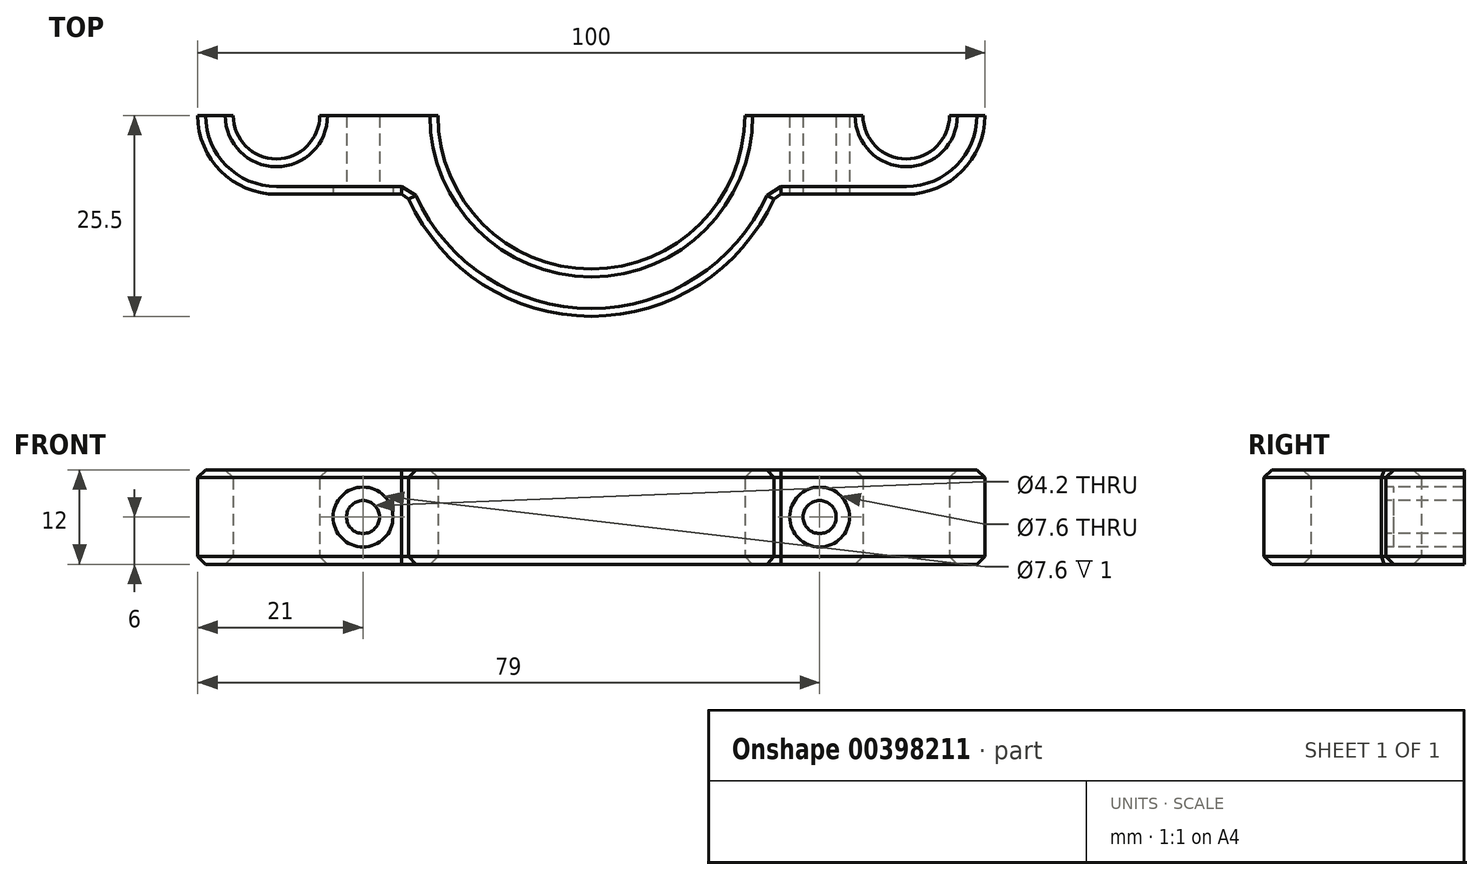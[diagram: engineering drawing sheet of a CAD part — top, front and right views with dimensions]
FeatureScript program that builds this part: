
annotation { "Feature Type Name" : "Feature", "Feature Type Description" : "" }
export const myFeature = defineFeature(function(context is Context, id is Id, definition is map)
    precondition{}
    {
        {
            var Q0;
            Q0=qCreatedBy(makeId("Top.planeOp"),FACE);
            var sketch = newSketch(context, id + "F0", { "sketchPlane" : qUnion([Q0])});
            skArc(sketch, "E0", {"start": v(-19.5, 0) * mm, "mid": v(0, -19.5) * mm, "end": v(19.5, 0) * mm});
            skArc(sketch, "E1", {"start": v(-50, 0) * mm, "mid": v(-47.07, -7.07) * mm, "end": v(-40, -10) * mm});
            skArc(sketch, "E2", {"start": v(-45.5, 0) * mm, "mid": v(-40, -5.5) * mm, "end": v(-34.5, 0) * mm});
            skArc(sketch, "E3.MirrorC", {"start": v(50, 0) * mm, "mid": v(47.07, -7.07) * mm, "end": v(40, -10) * mm});
            skArc(sketch, "E4.MirrorC", {"start": v(45.5, 0) * mm, "mid": v(40, -5.5) * mm, "end": v(34.5, 0) * mm});
            skArc(sketch, "E5", {"start": v(-23.46, -10) * mm, "mid": v(0, -25.5) * mm, "end": v(23.46, -10) * mm});
            skLineSegment(sketch, "E6", {"start": v(-40, -10) * mm, "end": v(-23.46, -10) * mm});
            skLineSegment(sketch, "E7", {"start": v(0, 0) * mm, "end": v(0, 37.42) * mm, "construction": true});
            skLineSegment(sketch, "E8.MirrorCS", {"start": v(40, -10) * mm, "end": v(23.46, -10) * mm});
            skLineSegment(sketch, "E9", {"start": v(-50, 0) * mm, "end": v(-45.5, 0) * mm});
            skLineSegment(sketch, "E10", {"start": v(-34.5, 0) * mm, "end": v(-19.5, 0) * mm});
            skLineSegment(sketch, "E11", {"start": v(19.5, 0) * mm, "end": v(34.5, 0) * mm});
            skLineSegment(sketch, "E12", {"start": v(45.5, 0) * mm, "end": v(50, 0) * mm});
            skSolve(sketch);
        }
        {
            var Q0;
            Q0=makeQuery(id+"F0.imprint","IMPRINT",FACE,{"disambiguationData":[TD([[makeQuery(id+"F0.imprint","IMPRINT",EDGE,{"derivedFrom":sQuery(id+"F0.wireOp",EDGE,"E0")}),-1.0]])]});
            var Q1;
            {var subQ0=sQuery(id+"F0.wireOp",EDGE,"9bc22d5b-6fa5-4b97-bc0c-ba3c2ce5b15b0.MirrorCS");var subQ1=sQuery(id+"F0.wireOp",EDGE,"E3.MirrorC");var subQ2=makeQuery(id+"F0.imprint","INTERSECT",VERTEX,{"derivedFrom":[subQ1,subQ0]});Q1=makeQuery(id+"F0.imprint","IMPRINT",FACE,{"disambiguationData":[TD([[makeQuery(id+"F0.imprint","IMPRINT",EDGE,{"disambiguationData":[TD([[subQ2,1.0]])],"derivedFrom":subQ1}),1.0]])]});}
            var Q2;
            {var subQ14=sQuery(id+"F0.wireOp",EDGE,"E3.MirrorC");var subQ15=makeQuery(id+"F0.imprint","INTERSECT",VERTEX,{"derivedFrom":[subQ14,sQuery(id+"F0.wireOp",EDGE,"9bc22d5b-6fa5-4b97-bc0c-ba3c2ce5b15b0.MirrorCS")]});Q2=makeQuery(id+"F0.imprint","IMPRINT",FACE,{"disambiguationData":[TD([[makeQuery(id+"F0.imprint","IMPRINT",EDGE,{"disambiguationData":[TD([[subQ15,-1.0]])],"derivedFrom":subQ14}),-1.0]])]});}
            var Q3;
            {var subQ0=sQuery(id+"F0.wireOp",EDGE,"c5e9826a-44c9-41ee-b3f6-7a52f2a30a6d0.MirrorCS");var subQ1=sQuery(id+"F0.wireOp",EDGE,"70cdf20a-ec98-4725-8234-b4e8db4446470.MirrorC");var subQ2=makeQuery(id+"F0.imprint","INTERSECT",VERTEX,{"disambiguationData":[OD(1.0)],"derivedFrom":[subQ1,subQ0]});Q3=makeQuery(id+"F0.imprint","IMPRINT",FACE,{"disambiguationData":[TD([[makeQuery(id+"F0.imprint","IMPRINT",EDGE,{"disambiguationData":[TD([[subQ2,-1.0]])],"derivedFrom":subQ1}),1.0]])]});}
            var Q4;
            {var subQ0=sQuery(id+"F0.wireOp",EDGE,"293a57c4-25d2-4a23-87fe-edfcddb039070.MirrorCS");var subQ1=sQuery(id+"F0.wireOp",EDGE,"70cdf20a-ec98-4725-8234-b4e8db4446470.MirrorC");var subQ2=makeQuery(id+"F0.imprint","INTERSECT",VERTEX,{"disambiguationData":[OD(1.0)],"derivedFrom":[subQ1,subQ0]});Q4=makeQuery(id+"F0.imprint","IMPRINT",FACE,{"disambiguationData":[TD([[makeQuery(id+"F0.imprint","IMPRINT",EDGE,{"disambiguationData":[TD([[subQ2,-1.0]])],"derivedFrom":subQ1}),1.0]])]});}
            var Q5;
            {var subQ0=sQuery(id+"F0.wireOp",EDGE,"8d17e300-eea9-4d37-96eb-c0b79c24fea70.MirrorCS");var subQ1=sQuery(id+"F0.wireOp",EDGE,"70cdf20a-ec98-4725-8234-b4e8db4446470.MirrorC");var subQ2=makeQuery(id+"F0.imprint","INTERSECT",VERTEX,{"disambiguationData":[OD(0.0)],"derivedFrom":[subQ1,subQ0]});Q5=makeQuery(id+"F0.imprint","IMPRINT",FACE,{"disambiguationData":[TD([[makeQuery(id+"F0.imprint","IMPRINT",EDGE,{"disambiguationData":[TD([[subQ2,1.0]])],"derivedFrom":subQ1}),1.0]])]});}
            var Q6;
            {var subQ0=sQuery(id+"F0.wireOp",EDGE,"8d17e300-eea9-4d37-96eb-c0b79c24fea70.MirrorCS");var subQ1=sQuery(id+"F0.wireOp",EDGE,"70cdf20a-ec98-4725-8234-b4e8db4446470.MirrorC");var subQ2=makeQuery(id+"F0.imprint","INTERSECT",VERTEX,{"disambiguationData":[OD(1.0)],"derivedFrom":[subQ1,subQ0]});Q6=makeQuery(id+"F0.imprint","IMPRINT",FACE,{"disambiguationData":[TD([[makeQuery(id+"F0.imprint","IMPRINT",EDGE,{"disambiguationData":[TD([[subQ2,-1.0]])],"derivedFrom":subQ1}),1.0]])]});}
            var Q7;
            {var subQ0=sQuery(id+"F0.wireOp",EDGE,"SkgDyUrd-1QQ2-iocv-R5lc-BY230uEkNkBm");var subQ1=sQuery(id+"F0.wireOp",EDGE,"E1");var subQ2=makeQuery(id+"F0.imprint","INTERSECT",VERTEX,{"derivedFrom":[subQ1,subQ0]});Q7=makeQuery(id+"F0.imprint","IMPRINT",FACE,{"disambiguationData":[TD([[makeQuery(id+"F0.imprint","IMPRINT",EDGE,{"disambiguationData":[TD([[subQ2,1.0]])],"derivedFrom":subQ1}),-1.0]])]});}
            var Q8;
            {var subQ0=sQuery(id+"F0.wireOp",EDGE,"osJs1pj3-h7Ac-X1eC-Lj8e-cso2r6UuOTxP.top");var subQ1=sQuery(id+"F0.wireOp",EDGE,"Qjw9ycuu-120G-4mMV-lDaF-yMnerR8b7inW");var subQ2=makeQuery(id+"F0.imprint","INTERSECT",VERTEX,{"disambiguationData":[OD(1.0)],"derivedFrom":[subQ1,subQ0]});Q8=makeQuery(id+"F0.imprint","IMPRINT",FACE,{"disambiguationData":[TD([[makeQuery(id+"F0.imprint","IMPRINT",EDGE,{"disambiguationData":[TD([[subQ2,-1.0]])],"derivedFrom":subQ1}),-1.0]])]});}
            var Q9;
            {var subQ0=sQuery(id+"F0.wireOp",EDGE,"osJs1pj3-h7Ac-X1eC-Lj8e-cso2r6UuOTxP.bottom");var subQ1=sQuery(id+"F0.wireOp",EDGE,"Qjw9ycuu-120G-4mMV-lDaF-yMnerR8b7inW");var subQ2=makeQuery(id+"F0.imprint","INTERSECT",VERTEX,{"disambiguationData":[OD(1.0)],"derivedFrom":[subQ1,subQ0]});Q9=makeQuery(id+"F0.imprint","IMPRINT",FACE,{"disambiguationData":[TD([[makeQuery(id+"F0.imprint","IMPRINT",EDGE,{"disambiguationData":[TD([[subQ2,-1.0]])],"derivedFrom":subQ1}),-1.0]])]});}
            var Q10;
            {var subQ0=sQuery(id+"F0.wireOp",EDGE,"osJs1pj3-h7Ac-X1eC-Lj8e-cso2r6UuOTxP.right");var subQ1=sQuery(id+"F0.wireOp",EDGE,"Qjw9ycuu-120G-4mMV-lDaF-yMnerR8b7inW");var subQ2=makeQuery(id+"F0.imprint","INTERSECT",VERTEX,{"disambiguationData":[OD(1.0)],"derivedFrom":[subQ1,subQ0]});Q10=makeQuery(id+"F0.imprint","IMPRINT",FACE,{"disambiguationData":[TD([[makeQuery(id+"F0.imprint","IMPRINT",EDGE,{"disambiguationData":[TD([[subQ2,-1.0]])],"derivedFrom":subQ1}),-1.0]])]});}
            var Q11;
            {var subQ0=sQuery(id+"F0.wireOp",EDGE,"osJs1pj3-h7Ac-X1eC-Lj8e-cso2r6UuOTxP.bottom");var subQ1=sQuery(id+"F0.wireOp",EDGE,"Qjw9ycuu-120G-4mMV-lDaF-yMnerR8b7inW");var subQ2=makeQuery(id+"F0.imprint","INTERSECT",VERTEX,{"disambiguationData":[OD(0.0)],"derivedFrom":[subQ1,subQ0]});Q11=makeQuery(id+"F0.imprint","IMPRINT",FACE,{"disambiguationData":[TD([[makeQuery(id+"F0.imprint","IMPRINT",EDGE,{"disambiguationData":[TD([[subQ2,1.0]])],"derivedFrom":subQ1}),-1.0]])]});}
            var Q12;
            {var subQ3=sQuery(id+"F0.wireOp",EDGE,"Qjw9ycuu-120G-4mMV-lDaF-yMnerR8b7inW");var subQ11=sQuery(id+"F0.wireOp",EDGE,"osJs1pj3-h7Ac-X1eC-Lj8e-cso2r6UuOTxP.bottom");var subQ12=makeQuery(id+"F0.imprint","INTERSECT",VERTEX,{"disambiguationData":[OD(0.0)],"derivedFrom":[subQ3,subQ11]});Q12=makeQuery(id+"F0.imprint","IMPRINT",FACE,{"disambiguationData":[TD([[makeQuery(id+"F0.imprint","IMPRINT",EDGE,{"disambiguationData":[TD([[subQ12,-1.0]])],"derivedFrom":subQ3}),-1.0]])]});}
            var Q13;
            Q13=makeQuery(id+"F0.imprint","IMPRINT",FACE,{"disambiguationData":[TD([[makeQuery(id+"F0.imprint","IMPRINT",EDGE,{"derivedFrom":sQuery(id+"F0.wireOp",EDGE,"Qjw9ycuu-120G-4mMV-lDaF-yMnerR8b7inW")}),-1.0]])]});
            var Q14;
            Q14=makeQuery(id+"F0.imprint","IMPRINT",FACE,{"disambiguationData":[TD([[makeQuery(id+"F0.imprint","IMPRINT",EDGE,{"derivedFrom":sQuery(id+"F0.wireOp",EDGE,"Qjw9ycuu-120G-4mMV-lDaF-yMnerR8b7inW")}),1.0]])]});
            var Q15;
            Q15=makeQuery(id+"F0.imprint","IMPRINT",FACE,{"disambiguationData":[TD([[makeQuery(id+"F0.imprint","IMPRINT",EDGE,{"derivedFrom":sQuery(id+"F0.wireOp",EDGE,"70cdf20a-ec98-4725-8234-b4e8db4446470.MirrorC")}),-1.0]])]});
            var Q16;
            {var subQ0=sQuery(id+"F0.wireOp",EDGE,"b66ebc68-1e64-4d65-8c2c-fe829603ed990.MirrorCS");Q16=makeQuery(id+"F0.imprint","IMPRINT",FACE,{"disambiguationData":[TD([[makeQuery(id+"F0.imprint","IMPRINT",EDGE,{"derivedFrom":subQ0}),-1.0]])]});}
            var Q17;
            {var subQ0=sQuery(id+"F0.wireOp",EDGE,"d2304aad-3bbf-496b-b2e4-f306b0abaab00.MirrorCS");Q17=makeQuery(id+"F0.imprint","IMPRINT",FACE,{"disambiguationData":[TD([[makeQuery(id+"F0.imprint","IMPRINT",EDGE,{"derivedFrom":subQ0}),1.0]])]});}
            extrude(context, id + "F1", {"entities" : qUnion([Q0, Q1, Q2, Q3, Q4, Q5, Q6, Q7, Q8, Q9, Q10, Q11, Q12, Q13, Q14, Q15, Q16, Q17]), "endBound" : BoundingType.SYMMETRIC, "depth" : 12 * mm, "offsetDistance" : 25 * mm});
        }
        {
            var Q0;
            Q0=makeQuery(id+"F1.opExtrude","SWEPT_FACE",FACE,{"disambiguationData":[OSD([sQuery(id+"F0.wireOp",EDGE,"E6")])]});
            cPlane(context, id + "F2", {"entities" : qUnion([Q0]), "cplaneType" : CPlaneType.OFFSET, "offset" : 0 * mm, "width" : 150 * mm, "height" : 150 * mm});
        }
        {
            var Q0;
            Q0=qCreatedBy(id+"F2.planeOp",FACE);
            var sketch = newSketch(context, id + "F3", { "sketchPlane" : qUnion([Q0])});
            skPoint(sketch, "E13", {"position": v(-29, 0) * mm});
            skCircle(sketch, "E14", {"center": v(-29, 0) * mm, "radius": 3.8 * mm});
            skCircle(sketch, "E15", {"center": v(-29, 0) * mm, "radius": 2.1 * mm});
            skLineSegment(sketch, "E16", {"start": v(0, 0) * mm, "end": v(0, 27.73) * mm, "construction": true});
            skCircle(sketch, "E17.MirrorC", {"center": v(29, 0) * mm, "radius": 3.8 * mm});
            skCircle(sketch, "E18.MirrorC", {"center": v(29, 0) * mm, "radius": 2.1 * mm});
            skSolve(sketch);
        }
        {
            var Q0;
            Q0=makeQuery(id+"F1.opExtrude","SWEPT_FACE",FACE,{"disambiguationData":[OSD([sQuery(id+"F0.wireOp",EDGE,"E5")])]});
            var Q1;
            Q1=makeQuery(id+"F1.opExtrude","CAP_EDGE",EDGE,{"disambiguationData":[OSD([sQuery(id+"F0.wireOp",EDGE,"E2")])],"isStart":false});
            var Q2;
            Q2=makeQuery(id+"F1.opExtrude","CAP_EDGE",EDGE,{"disambiguationData":[OSD([sQuery(id+"F0.wireOp",EDGE,"E2")])],"isStart":true});
            var Q3;
            Q3=makeQuery(id+"F1.opExtrude","CAP_EDGE",EDGE,{"disambiguationData":[OSD([sQuery(id+"F0.wireOp",EDGE,"E4.MirrorC")])],"isStart":false});
            var Q4;
            Q4=makeQuery(id+"F1.opExtrude","CAP_EDGE",EDGE,{"disambiguationData":[OSD([sQuery(id+"F0.wireOp",EDGE,"E4.MirrorC")])],"isStart":true});
            var Q5;
            Q5=makeQuery(id+"F1.opExtrude","CAP_EDGE",EDGE,{"disambiguationData":[OSD([sQuery(id+"F0.wireOp",EDGE,"E0")])],"isStart":true});
            var Q6;
            Q6=makeQuery(id+"F1.opExtrude","CAP_EDGE",EDGE,{"disambiguationData":[OSD([sQuery(id+"F0.wireOp",EDGE,"E0")])],"isStart":false});
            chamfer(context, id + "F4", {"entities" : qUnion([Q0, Q1, Q2, Q3, Q4, Q5, Q6]), "width" : 1 * mm, "tangentPropagation" : true});
        }
        {
            var Q0;
            Q0=makeQuery(id+"F3.imprint","IMPRINT",FACE,{"disambiguationData":[TD([[makeQuery(id+"F3.imprint","IMPRINT",EDGE,{"derivedFrom":sQuery(id+"F3.wireOp",EDGE,"E15")}),1.0]])]});
            var Q1;
            Q1=makeQuery(id+"F3.imprint","IMPRINT",FACE,{"disambiguationData":[TD([[makeQuery(id+"F3.imprint","IMPRINT",EDGE,{"derivedFrom":sQuery(id+"F3.wireOp",EDGE,"E18.MirrorC")}),-1.0]])]});
            extrude(context, id + "F5", {"entities" : qUnion([Q0, Q1]), "operationType" : NewBodyOperationType.REMOVE, "oppositeDirection" : true, "depth" : 25 * mm, "offsetDistance" : 25 * mm});
        }
        {
            var Q0;
            Q0=makeQuery(id+"F3.imprint","IMPRINT",FACE,{"disambiguationData":[TD([[makeQuery(id+"F3.imprint","IMPRINT",EDGE,{"derivedFrom":sQuery(id+"F3.wireOp",EDGE,"E14")}),1.0]])]});
            var Q1;
            Q1=makeQuery(id+"F3.imprint","IMPRINT",FACE,{"disambiguationData":[TD([[makeQuery(id+"F3.imprint","IMPRINT",EDGE,{"derivedFrom":sQuery(id+"F3.wireOp",EDGE,"E17.MirrorC")}),-1.0]])]});
            extrude(context, id + "F6", {"entities" : qUnion([Q0, Q1]), "operationType" : NewBodyOperationType.REMOVE, "flatOperationType" : FlatOperationType.REMOVE, "oppositeDirection" : true, "depth" : 1 * mm, "offsetDistance" : 25 * mm, "domain" : OperationDomain.MODEL});
        }
    });
